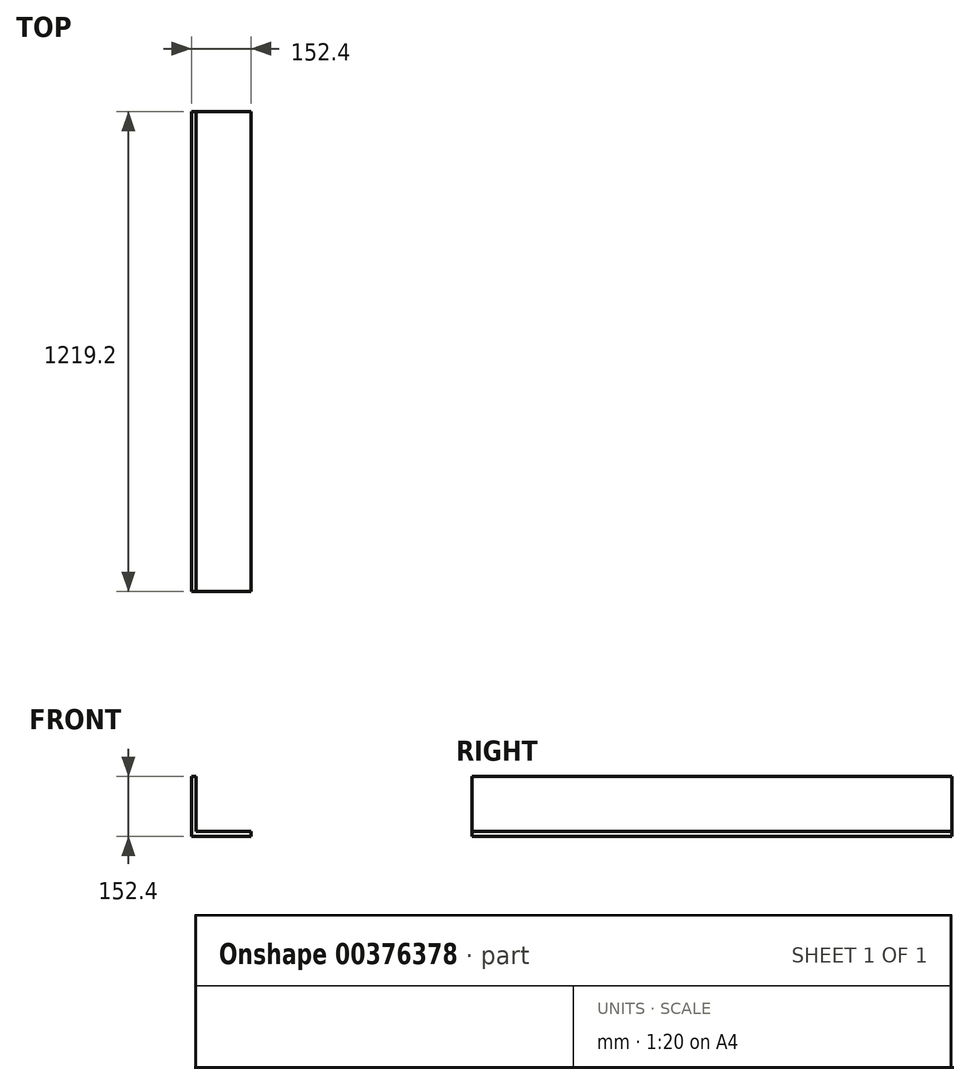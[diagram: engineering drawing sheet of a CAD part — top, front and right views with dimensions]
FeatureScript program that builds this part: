
annotation { "Feature Type Name" : "Feature", "Feature Type Description" : "" }
export const myFeature = defineFeature(function(context is Context, id is Id, definition is map)
    precondition{}
    {
        {
            var Q0;
            Q0=qCreatedBy(makeId("Front.planeOp"),FACE);
            var sketch = newSketch(context, id + "F0", { "sketchPlane" : qUnion([Q0])});
            skLineSegment(sketch, "E0", {"start": v(0, 0) * mm, "end": v(0, 152.4) * mm});
            skLineSegment(sketch, "E1", {"start": v(0, 152.4) * mm, "end": v(12.7, 152.4) * mm});
            skLineSegment(sketch, "E2", {"start": v(12.7, 152.4) * mm, "end": v(12.7, 12.7) * mm});
            skLineSegment(sketch, "E3", {"start": v(12.7, 12.7) * mm, "end": v(152.4, 12.7) * mm});
            skLineSegment(sketch, "E4", {"start": v(152.4, 12.7) * mm, "end": v(152.4, 0) * mm});
            skLineSegment(sketch, "E5", {"start": v(152.4, 0) * mm, "end": v(0, 0) * mm});
            skSolve(sketch);
        }
        {
            var Q0;
            Q0 = qSketchRegion(id + "F0", true);
            extrude(context, id + "F1", {"entities" : qUnion([Q0]), "depth" : 1219.2 * mm});
        }
        {
            var Q0;
            Q0=makeQuery(id+"F1.opExtrude","SWEPT_FACE",FACE,{"disambiguationData":[OSD([sQuery(id+"F0.wireOp",EDGE,"E2")])]});
            var sketch = newSketch(context, id + "F2", { "sketchPlane" : qUnion([Q0])});
            skSolve(sketch);
        }
    });
